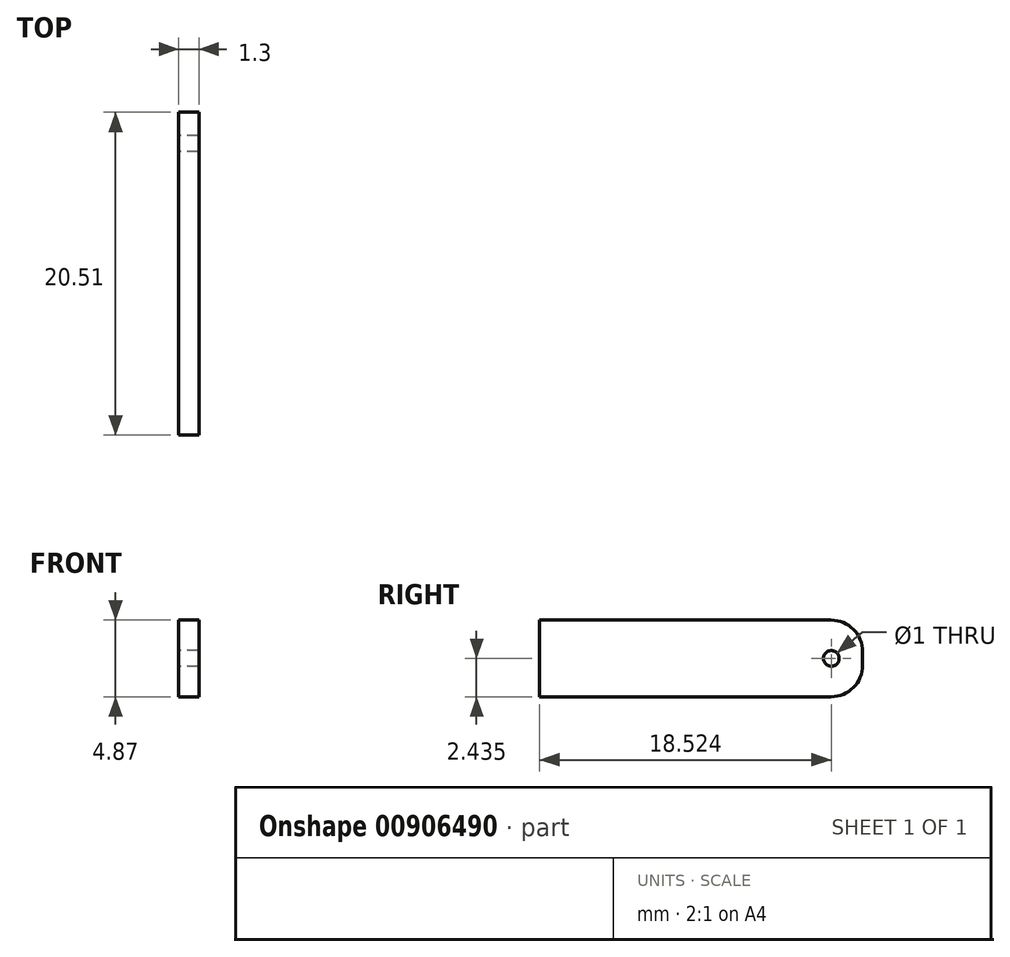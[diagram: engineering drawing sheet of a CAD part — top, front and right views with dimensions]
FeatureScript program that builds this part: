
annotation { "Feature Type Name" : "Feature", "Feature Type Description" : "" }
export const myFeature = defineFeature(function(context is Context, id is Id, definition is map)
    precondition{}
    {
        {
            var Q0;
            Q0=qCreatedBy(makeId("Right.planeOp"),FACE);
            var sketch = newSketch(context, id + "F0", { "sketchPlane" : qUnion([Q0])});
            skLineSegment(sketch, "E0.bottom", {"start": v(0, 0) * mm, "end": v(18.51, 0) * mm});
            skLineSegment(sketch, "E0.top", {"start": v(0, -4.87) * mm, "end": v(18.51, -4.87) * mm});
            skLineSegment(sketch, "E0.left", {"start": v(0, 0) * mm, "end": v(0, -4.87) * mm});
            skLineSegment(sketch, "E0.right", {"start": v(20.51, -2) * mm, "end": v(20.51, -2.87) * mm});
            skPoint(sketch, "E1.visualSharp", {"position": v(20.51, 0) * mm});
            skArc(sketch, "E1.filletArc", {"start": v(20.51, -2) * mm, "mid": v(19.93, -0.59) * mm, "end": v(18.51, 0) * mm});
            skPoint(sketch, "E2.visualSharp", {"position": v(20.51, -4.87) * mm});
            skArc(sketch, "E2.filletArc", {"start": v(18.51, -4.87) * mm, "mid": v(19.93, -4.28) * mm, "end": v(20.51, -2.87) * mm});
            skCircle(sketch, "E3", {"center": v(18.52, -2.43) * mm, "radius": 0.5 * mm});
            skPoint(sketch, "E3.centerSnap0", {"position": v(20.51, -2.43) * mm});
            skSolve(sketch);
        }
        {
            var Q0;
            Q0=makeQuery(id+"F0.imprint","IMPRINT",FACE,{"disambiguationData":[TD([[makeQuery(id+"F0.imprint","IMPRINT",EDGE,{"derivedFrom":sQuery(id+"F0.wireOp",EDGE,"E0.bottom")}),-1.0]])]});
            extrude(context, id + "F1", {"entities" : qUnion([Q0]), "depth" : 1.3 * mm, "offsetDistance" : 25 * mm});
        }
    });
